# Revit family: F1100-C-PLA
name_source: partatom
category: Plumbing Fixtures
revit_build: Autodesk Revit 2017 (Build: 20190508_0315(x64)
units: mm (PartAtom-declared; Revit-internal decimal feet)

## family parameters
Cut with Voids When Loaded = No
Host = Face
Part Type = Normal
Room Calculation Point = No
Round Connector Dimension = Use Radius
Shared = No

## types (5) — shared parameters
Body Height = 0' - 3 1/2"
Default Elevation = 0' - 0"
Description = PODIUM DRAINS
Domestic Cold Water Diameter = 0' - 0 1/2"
Domestic Cold Water Radius = 0' - 0 1/2"
Floor Drain Material = Paint - Sherwin Williams Paint - #952C2A - Bellwood Red
Manufacturer = MIFAB
Model = F1100-C-PLA
Strainer Diameter = 0' - 7"
URL = WWW.MIFAB.COM
zero-valued in all types: CWFU, WFU

## per-type parameters (varying)
| type | Diameter | Pipe Diameter | Pipe Radius |
| 5" Dia  Strainer - 2" Drain | 0' - 5" | 0' - 2" | 0' - 1" |
| 6" Dia  Strainer - 3" Drain | 0' - 6" | 0' - 3" | 0' - 1 1/2" |
| 7" Dia  Strainer - 4" Drain | 0' - 7" | 0' - 4" | 0' - 2" |
| 8" Dia  Strainer - 5" Drain | 0' - 8" | 0' - 5" | 0' - 2 1/2" |
| 10" Dia  Strainer - 6" Drain | 0' - 10" | 0' - 6" | 0' - 3" |

## geometry (parser evidence)
native form markers: Blend x4, Sweep x5
no freeform markers — native parametric forms only
